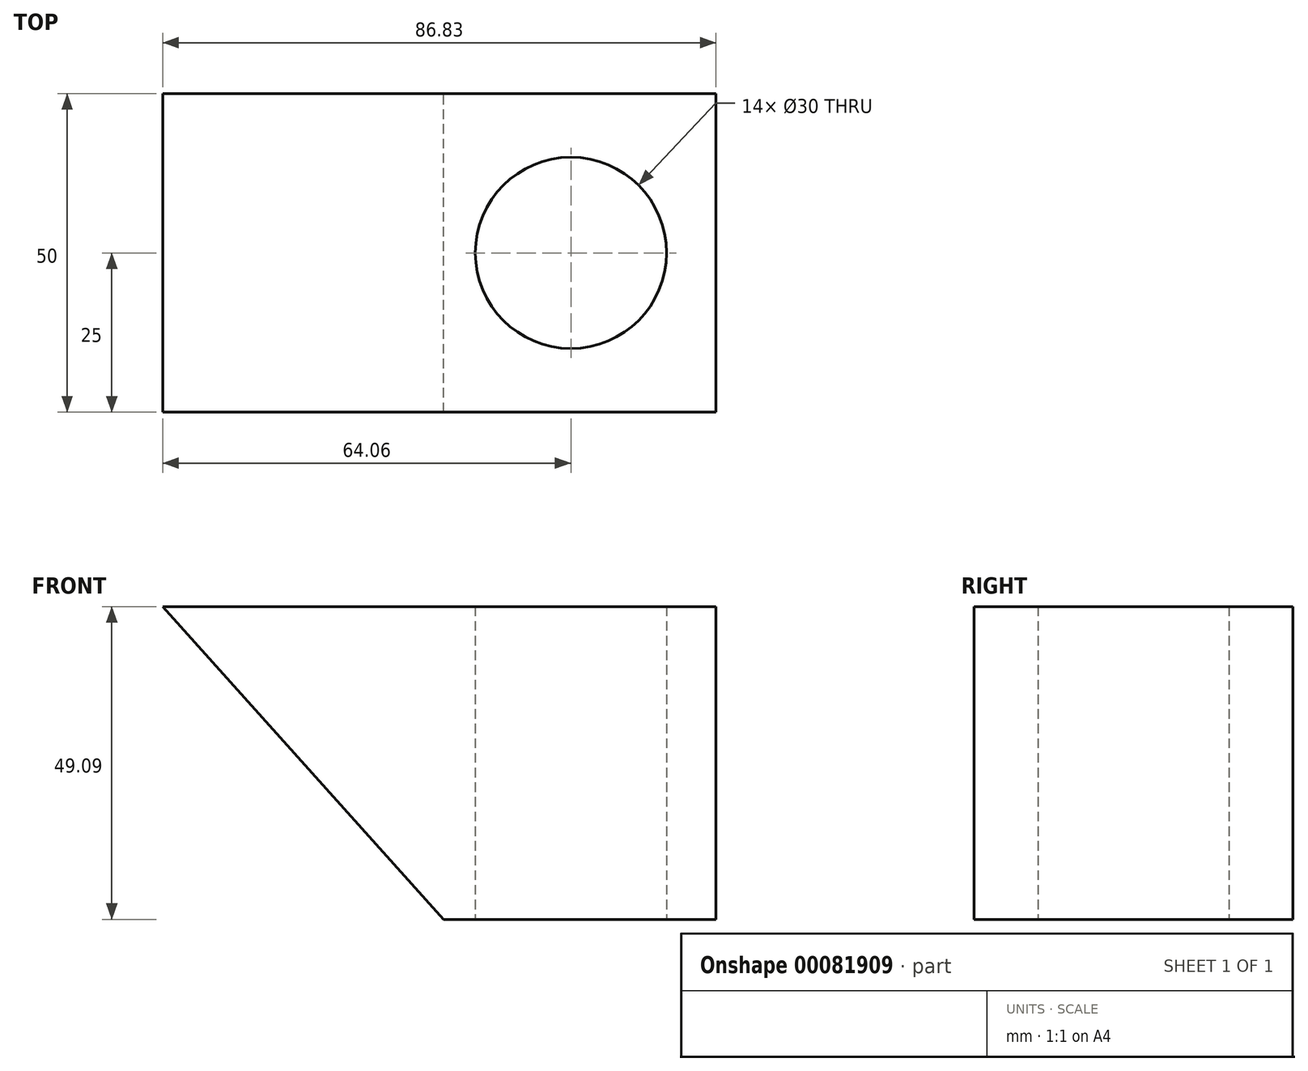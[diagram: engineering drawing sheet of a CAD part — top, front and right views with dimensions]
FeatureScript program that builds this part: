
annotation { "Feature Type Name" : "Feature", "Feature Type Description" : "" }
export const myFeature = defineFeature(function(context is Context, id is Id, definition is map)
    precondition{}
    {
        {
            var Q0;
            Q0=qCreatedBy(makeId("Front.planeOp"),FACE);
            var sketch = newSketch(context, id + "F0", { "sketchPlane" : qUnion([Q0])});
            skLineSegment(sketch, "E0", {"start": v(0, 0) * mm, "end": v(42.77, 0) * mm});
            skLineSegment(sketch, "E1", {"start": v(42.77, 0) * mm, "end": v(42.77, 49.09) * mm});
            skLineSegment(sketch, "E2", {"start": v(42.77, 49.09) * mm, "end": v(-44.06, 49.09) * mm});
            skLineSegment(sketch, "E3", {"start": v(-44.06, 49.09) * mm, "end": v(0, 0) * mm});
            skSolve(sketch);
        }
        {
            var Q0;
            Q0 = qSketchRegion(id + "F0", true);
            extrude(context, id + "F1", {"entities" : qUnion([Q0]), "endBound" : BoundingType.SYMMETRIC, "depth" : 50 * mm});
        }
        {
            var Q0;
            Q0=makeQuery(id+"F1.opExtrude","SWEPT_FACE",FACE,{"disambiguationData":[OSD([sQuery(id+"F0.wireOp",EDGE,"E0")])]});
            var sketch = newSketch(context, id + "F2", { "sketchPlane" : qUnion([Q0])});
            skCircle(sketch, "E4", {"center": v(20, 0) * mm, "radius": 15 * mm});
            skSolve(sketch);
        }
        {
            var Q0;
            Q0 = qSketchRegion(id + "F2", true);
            extrude(context, id + "F3", {"entities" : qUnion([Q0]), "operationType" : NewBodyOperationType.REMOVE, "endBound" : BoundingType.THROUGH_ALL, "oppositeDirection" : true, "depth" : 25 * mm});
        }
    });
